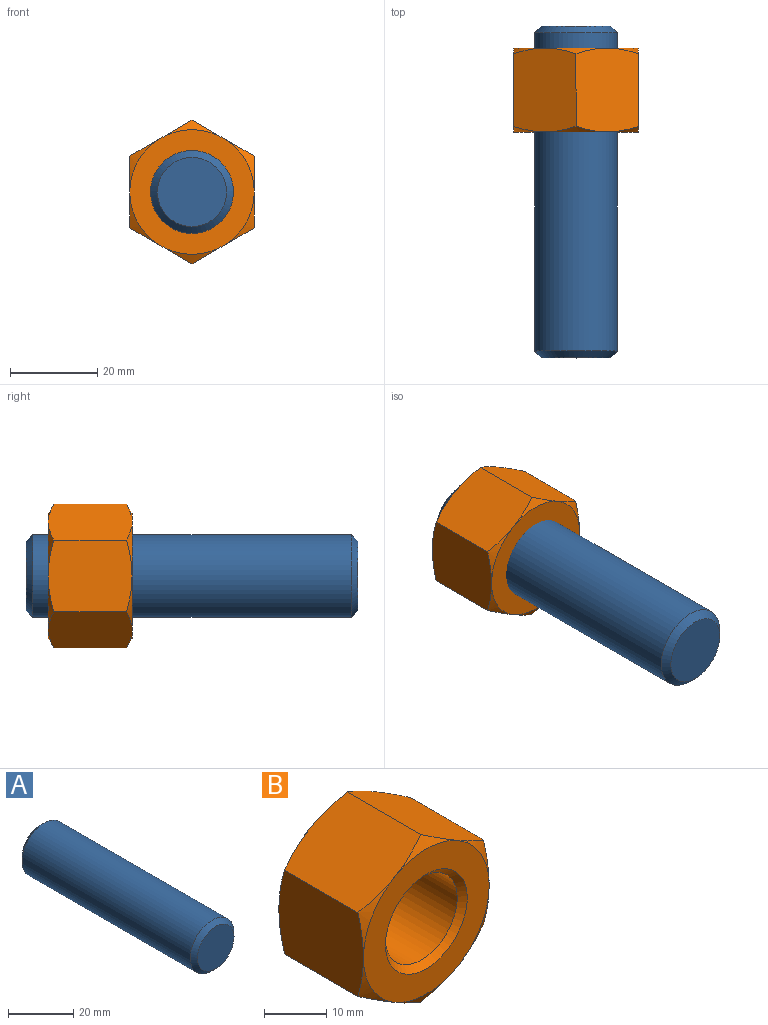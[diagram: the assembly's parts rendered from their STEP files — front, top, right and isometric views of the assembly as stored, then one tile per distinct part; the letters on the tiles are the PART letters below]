
ASSEMBLY  parts=2 mates=2
PART A: 5 faces, bbox 19.1x76.2x19.1 mm
  f0: cylinder r=9.53mm len=73.03mm, axis (0,-1,0), area 4370.4mm2, adj f3,f4
  f1: plane 15.88x15.88mm, normal (0,1,0), area 197.9mm2, adj f3
  f2: plane 15.88x15.88mm, normal (0,-1,0), area 197.9mm2, adj f4
  f3: cone r=9.53mm half-angle=45deg, axis (0,-1,0), area 123.2mm2, adj f0,f1
  f4: cone r=7.94mm half-angle=45deg, axis (0,1,0), area 123.2mm2, adj f0,f2
PART B: 23 faces, bbox 33x19.3x33 mm
  f0: cylinder r=8.15mm len=16.97mm, axis (0,-1,0), area 869.2mm2, adj f21,f22
  f1: plane 28.58x28.58mm, normal (0,1,0), area 369.8mm2, adj f3,f4,f7,f9,f11,f13,f21
  f2: plane 28.58x28.58mm, normal (0,-1,0), area 369.8mm2, adj f5,f6,f8,f10,f12,f14,f22
  f3: cone r=14.29mm half-angle=60deg, axis (0,-1,0), area 12.7mm2, adj f1,f15,f20
  f4: cone r=14.29mm half-angle=60deg, axis (0,-1,0), area 12.7mm2, adj f1,f15,f16
  f5: cone r=14.29mm half-angle=60deg, axis (0,1,0), area 12.7mm2, adj f2,f15,f20
  f6: cone r=14.29mm half-angle=60deg, axis (0,1,0), area 12.7mm2, adj f2,f15,f16
  f7: cone r=14.29mm half-angle=60deg, axis (0,-1,0), area 12.7mm2, adj f1,f16,f17
  f8: cone r=14.29mm half-angle=60deg, axis (0,1,0), area 12.7mm2, adj f2,f16,f17
  f9: cone r=14.29mm half-angle=60deg, axis (0,-1,0), area 12.7mm2, adj f1,f17,f18
  f10: cone r=14.29mm half-angle=60deg, axis (0,1,0), area 12.7mm2, adj f2,f17,f18
  f11: cone r=14.29mm half-angle=60deg, axis (0,-1,0), area 12.7mm2, adj f1,f18,f19
  f12: cone r=14.29mm half-angle=60deg, axis (0,1,0), area 12.7mm2, adj f2,f18,f19
  f13: cone r=14.29mm half-angle=60deg, axis (0,-1,0), area 12.7mm2, adj f1,f19,f20
  f14: cone r=14.29mm half-angle=60deg, axis (0,1,0), area 12.7mm2, adj f2,f19,f20
  f15: plane 19.26x14.29mm, normal (-0.5,0,-0.87), area 303.2mm2, adj f3,f4,f5,f6,f16,f20
  f16: plane 19.26x16.51mm, normal (-1,0,0), area 303.2mm2, adj f4,f6,f7,f8,f15,f17
  f17: plane 19.26x14.29mm, normal (-0.5,0,0.87), area 303.2mm2, adj f7,f8,f9,f10,f16,f18
  f18: plane 19.26x14.29mm, normal (0.5,0,0.87), area 303.2mm2, adj f9,f10,f11,f12,f17,f19
  f19: plane 19.26x16.51mm, normal (1,0,0), area 303.2mm2, adj f11,f12,f13,f14,f18,f20
  f20: plane 19.26x14.29mm, normal (0.5,0,-0.87), area 303.2mm2, adj f3,f5,f13,f14,f15,f19
  f21: cone r=9.3mm half-angle=45deg, axis (0,1,0), area 88.6mm2, adj f0,f1
  f22: cone r=8.15mm half-angle=45deg, axis (0,-1,0), area 88.6mm2, adj f0,f2
PLACE A t=(-9.36,-26.83,-7.24)mm
PLACE B t=(-9.36,25.04,-7.24)mm
MATE cylindrical A.f0 <-> B.f0  axis (0,-1,0) through (-9.36,11.27,-7.24)mm
MATE planar B.f3 <-> A.f0  axis (0,1,0) through (-9.36,44.29,-7.24)mm
